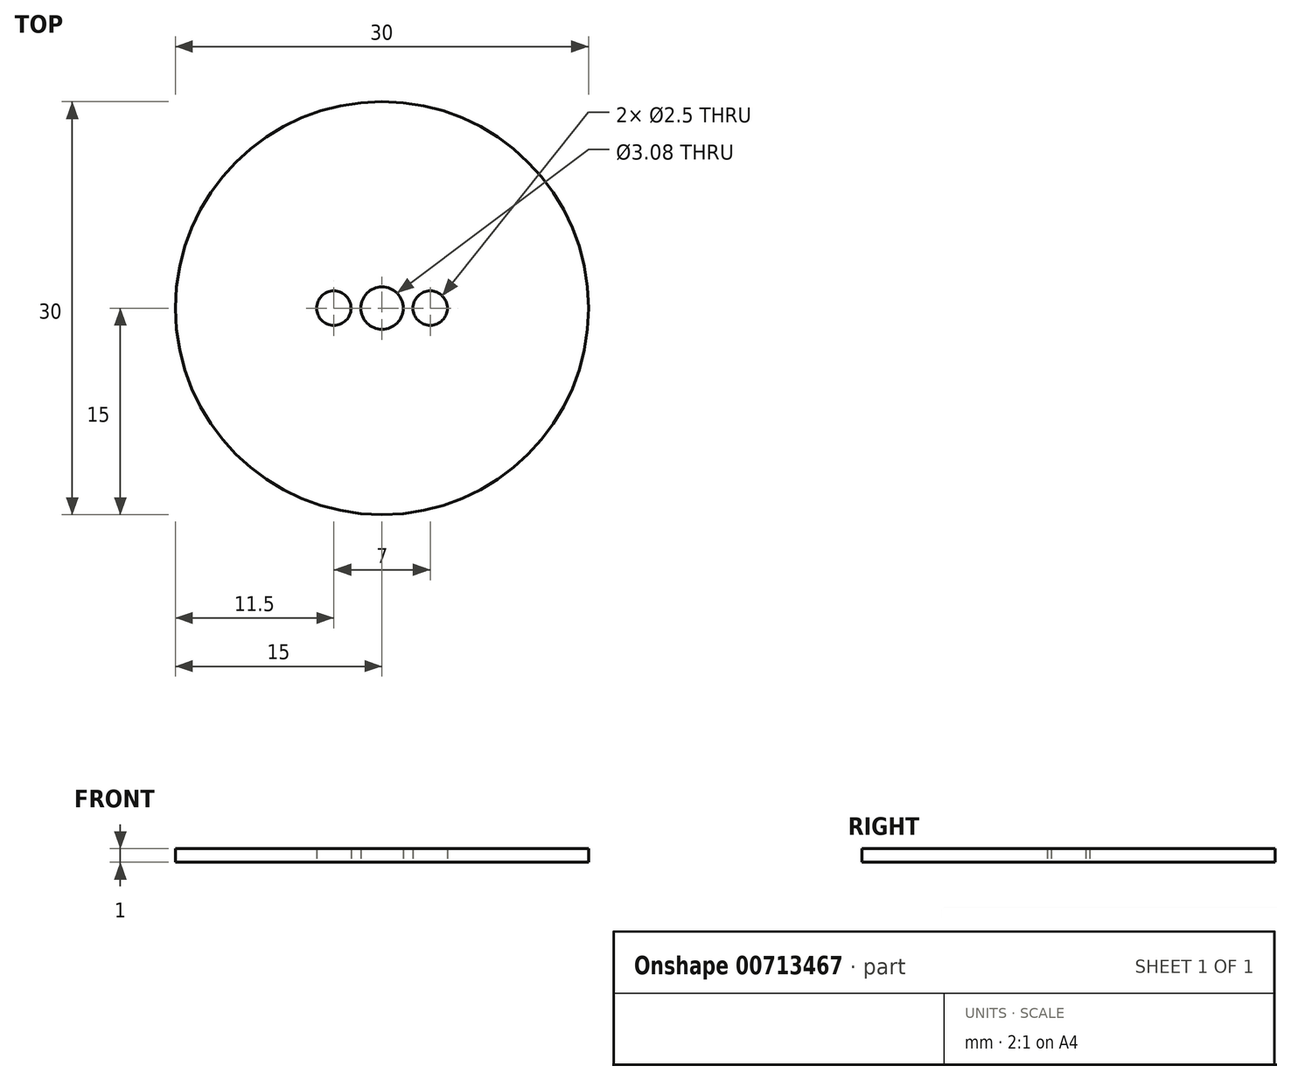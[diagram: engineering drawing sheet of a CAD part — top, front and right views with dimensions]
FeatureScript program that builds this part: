
annotation { "Feature Type Name" : "Feature", "Feature Type Description" : "" }
export const myFeature = defineFeature(function(context is Context, id is Id, definition is map)
    precondition{}
    {
        {
            var Q0;
            Q0=qCreatedBy(makeId("Top.planeOp"),FACE);
            var sketch = newSketch(context, id + "F0", { "sketchPlane" : qUnion([Q0])});
            skCircle(sketch, "E0", {"center": v(0, 0) * mm, "radius": 15 * mm});
            skCircle(sketch, "E1", {"center": v(0, 0) * mm, "radius": 1.54 * mm});
            skCircle(sketch, "E2", {"center": v(3.5, 0) * mm, "radius": 1.25 * mm});
            skLineSegment(sketch, "E3", {"start": v(0, 0) * mm, "end": v(0, 11.59) * mm, "construction": true});
            skCircle(sketch, "E4.MirrorC", {"center": v(-3.5, 0) * mm, "radius": 1.25 * mm});
            skSolve(sketch);
        }
        {
            var Q0;
            Q0=qSketchRegion(id+"F0",true);
            extrude(context, id + "F1", {"entities" : qUnion([Q0]), "depth" : 1 * mm, "offsetDistance" : 25 * mm});
        }
    });
